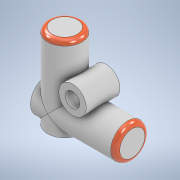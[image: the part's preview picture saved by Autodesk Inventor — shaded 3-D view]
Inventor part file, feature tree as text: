
AUTODESK INVENTOR PART (.ipt)
format: ipt  version: 2021 (Build 250183000, 183)  size: 173,568 bytes
history: native  units: mm
features: extrude x3, sketch x3, projected_geometry x2, fillet x1
ambient origin geometry x8: Origin, YZ Plane, XZ Plane, XY Plane, X Axis, Y Axis, Z Axis, Center Point
bodies: Solid1 (feature_tree)
feature tree (9):
  extrude  "Extrusion1"  Depth=18.4mm TaperAngle=0.0deg
  extrude  "Extrusion2"  Depth=3.75mm TaperAngle=0.0deg
  extrude  "Extrusion3"  Depth=1.0mm
  fillet  "Fillet1"  Radius=3.2mm
  sketch  "Sketch1"  dims[d0=7.5mm d1=18.4mm d2=0.0mm]
  sketch  "Sketch2"  dims[d3=7.5mm d4=14.8mm d5=3.75mm d6=0.0mm d7=0.0mm]
  sketch  "Sketch3"  dims[d8=5.4mm d9=5.4mm d10=3.2mm d11=6.0mm d12=7.4mm d13=0.0mm d14=1.0mm]
  projected_geometry  "Projected Loop1"
  projected_geometry  "Projected Loop2"
